# Revit family: Deca_Misturador Lavatório Wish_1877.C.WSH_Mesa Bica Alta
name_source: partatom
category: Plumbing Fixtures
revit_build: Autodesk Revit Architecture 2012 (Build: 20120126_0600(x64)
units: mm (PartAtom-declared; Revit-internal decimal feet)

## types (2) — shared parameters
Acompanha o Produto = Válvula de escoamento 1601.C
Aprovado por = Contino/quattroD
Assembly Code = D2020
Atendimento ao Cliente = 0800-0117073
Consumo = Varia com a pressão
Criado por = Contino/quattroD
Description = Misturador lavatório mesa
Diâmetro Água Fria = 15 mm  [stored 0.0492126 ft]
Diâmetro Água Quente = 15 mm  [stored 0.0492126 ft]
Flow Pressure = 0.00 psi
Informações Complementares = Mecanismo: 1/4 volta
Linha = Wish
Louça/Metais = Metal
Manufacturer = Deca
Material = Deca_Latão Cromado e Plástico de Engenharia
Norma = ABNT NBR 14390: 2001
Peso Liquido (Kg) = 2.63
Pressão = 2 A 40 mca
Produto = Misturador lavatório mesa bica alta Wish
Raio Água Fria = 8 mm  [stored 0.0262467 ft]
Raio Água Quente = 8 mm  [stored 0.0262467 ft]
Segmento = Luxo
URL = www.deca.com.br/produtos
Variações de COR = Cromado (1877.C.WSH); Gold (1877.D.WSH.GLD)
Vendido Separadamente = Ligação Flexível: 30 cm (4607.C.030), 40 cm (4607.C.040), 50 cm (4607.C.050).
zero-valued in all types: CWFU, Default Elevation, HWFU, WFU

## per-type parameters (varying)
| type | Código | Misturador | Model |
| 1877.C.WSH_Cromado CR10 | 1877.C.WSH | Deca CR10 Cromado Metal | 1877.C.WSH |
| 1877.D.WSH.GLD_Gold GLD | 1877.D.WSH.GLD | Deca GLD Gold Metal | 1877.D.WSH.GLD |

note: [stored X ft] marks values corroborated as IEEE doubles in the binary element streams (Revit-internal decimal feet)

## geometry (parser evidence)
native form markers: Blend x4, Sweep x2
no freeform markers — native parametric forms only
